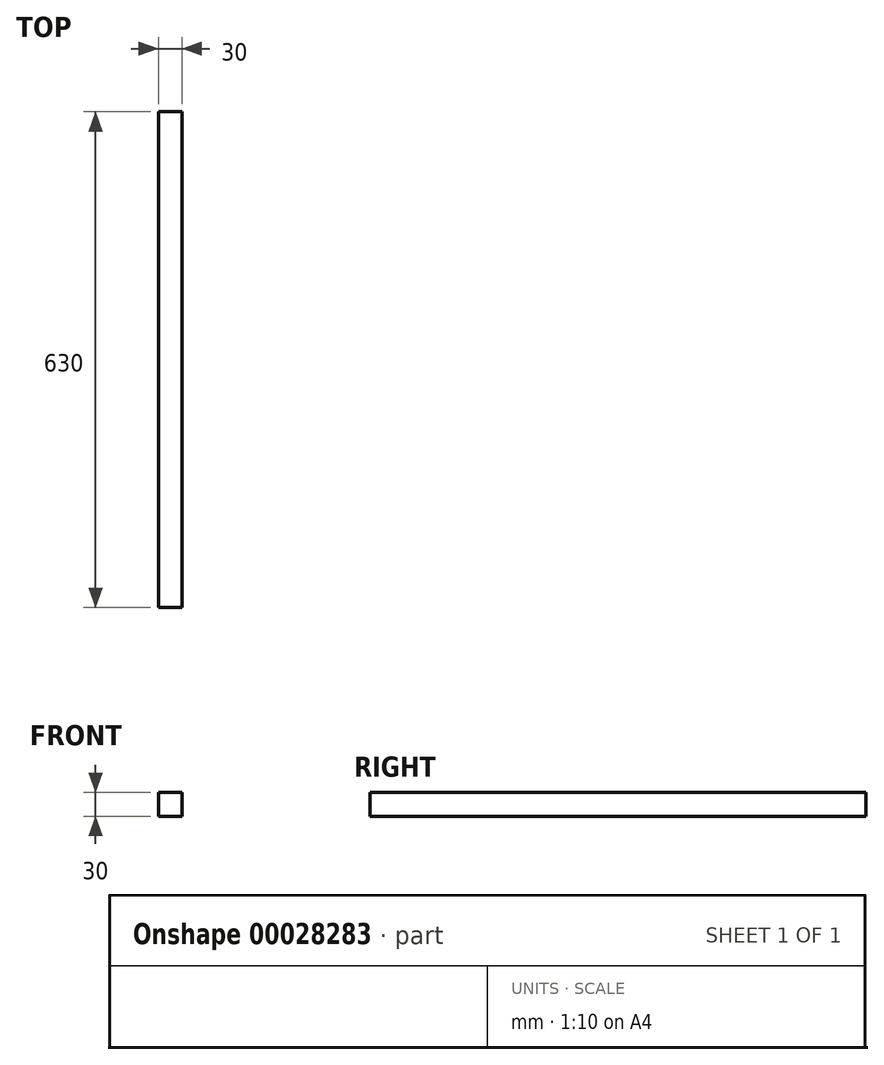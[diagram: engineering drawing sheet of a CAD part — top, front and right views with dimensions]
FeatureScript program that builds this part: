
annotation { "Feature Type Name" : "Feature", "Feature Type Description" : "" }
export const myFeature = defineFeature(function(context is Context, id is Id, definition is map)
    precondition{}
    {
        {
            var Q0;
            Q0=qCreatedBy(makeId("Front.planeOp"),FACE);
            var sketch = newSketch(context, id + "F0", { "sketchPlane" : qUnion([Q0])});
            skLineSegment(sketch, "E0.bottom", {"start": v(0, 0) * mm, "end": v(30, 0) * mm});
            skLineSegment(sketch, "E0.top", {"start": v(0, -30) * mm, "end": v(30, -30) * mm});
            skLineSegment(sketch, "E0.left", {"start": v(0, 0) * mm, "end": v(0, -30) * mm});
            skLineSegment(sketch, "E0.right", {"start": v(30, 0) * mm, "end": v(30, -30) * mm});
            skSolve(sketch);
        }
        {
            var Q0;
            Q0 = qSketchRegion(id + "F0", true);
            extrude(context, id + "F1", {"entities" : qUnion([Q0]), "depth" : 630 * mm});
        }
    });
